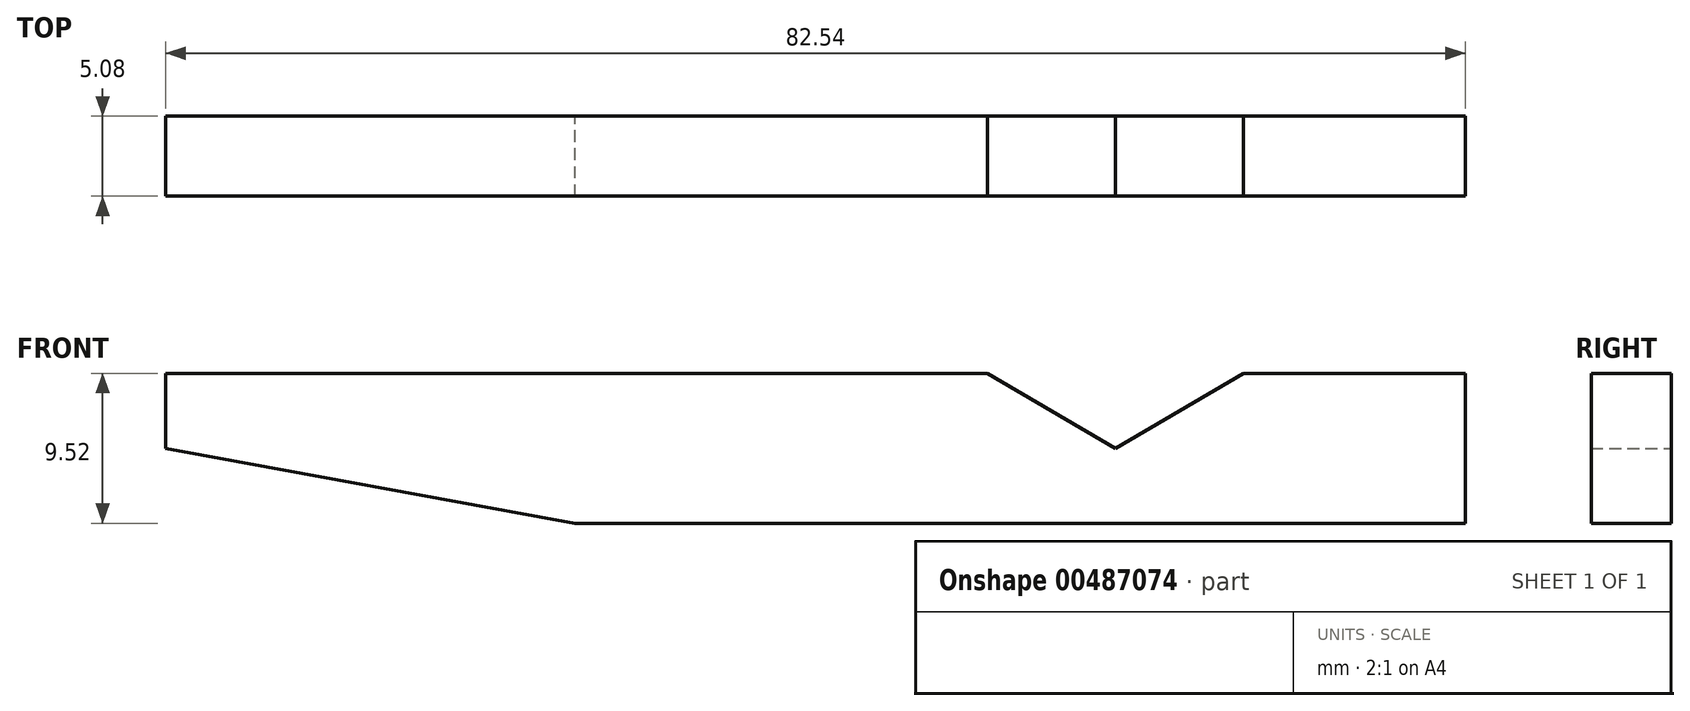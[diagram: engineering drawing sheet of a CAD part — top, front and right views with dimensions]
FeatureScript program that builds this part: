
annotation { "Feature Type Name" : "Feature", "Feature Type Description" : "" }
export const myFeature = defineFeature(function(context is Context, id is Id, definition is map)
    precondition{}
    {
        {
            var Q0;
            Q0=qCreatedBy(makeId("Front.planeOp"),FACE);
            var sketch = newSketch(context, id + "F0", { "sketchPlane" : qUnion([Q0])});
            skLineSegment(sketch, "E0.bottom", {"start": v(-41.28, 4.76) * mm, "end": v(10.92, 4.76) * mm});
            skLineSegment(sketch, "E0.top", {"start": v(-15.27, -4.76) * mm, "end": v(41.28, -4.76) * mm});
            skLineSegment(sketch, "E0.left", {"start": v(-41.28, 4.76) * mm, "end": v(-41.28, 0) * mm});
            skLineSegment(sketch, "E0.right", {"start": v(41.28, 4.76) * mm, "end": v(41.28, -4.76) * mm});
            skPoint(sketch, "E0.middle", {"position": v(0, 0) * mm});
            skLineSegment(sketch, "E1", {"start": v(-41.28, 0) * mm, "end": v(-15.27, -4.76) * mm});
            skLineSegment(sketch, "E2", {"start": v(10.92, 4.76) * mm, "end": v(19.05, 0) * mm});
            skLineSegment(sketch, "E3", {"start": v(19.05, 0) * mm, "end": v(27.18, 4.76) * mm});
            skLineSegment(sketch, "E4.trimOffspring", {"start": v(27.18, 4.76) * mm, "end": v(41.28, 4.76) * mm});
            skSolve(sketch);
        }
        {
            var Q0;
            Q0=makeQuery(id+"F0.imprint","IMPRINT",FACE,{"disambiguationData":[TD([[makeQuery(id+"F0.imprint","IMPRINT",EDGE,{"derivedFrom":sQuery(id+"F0.wireOp",EDGE,"E0.bottom")}),-1.0]])]});
            extrude(context, id + "F1", {"entities" : qUnion([Q0]), "depth" : 5.08 * mm});
        }
    });
